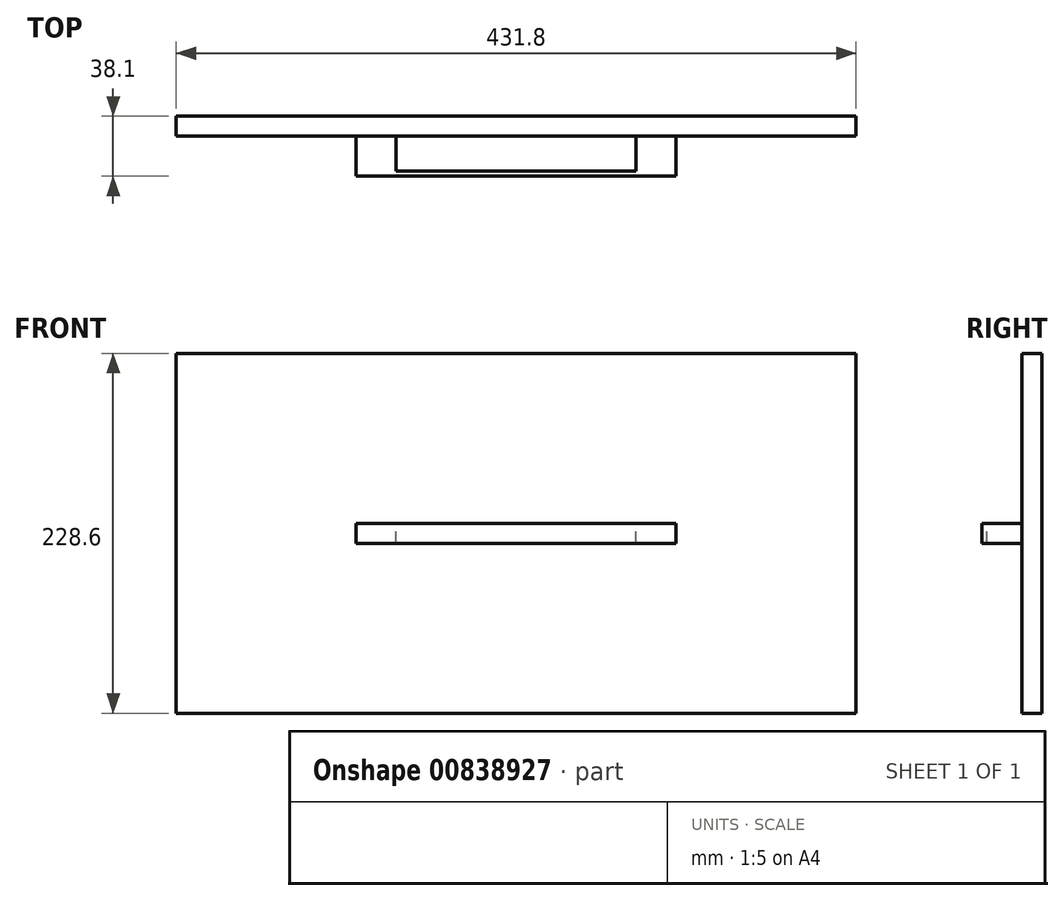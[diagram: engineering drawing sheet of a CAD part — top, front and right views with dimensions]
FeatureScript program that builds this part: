
annotation { "Feature Type Name" : "Feature", "Feature Type Description" : "" }
export const myFeature = defineFeature(function(context is Context, id is Id, definition is map)
    precondition{}
    {
        {
            var Q0;
            Q0=qCreatedBy(makeId("Front.planeOp"),FACE);
            var sketch = newSketch(context, id + "F0", { "sketchPlane" : qUnion([Q0])});
            skLineSegment(sketch, "E0", {"start": v(0, 0) * mm, "end": v(0, 228.6) * mm});
            skLineSegment(sketch, "E1", {"start": v(0, 228.6) * mm, "end": v(431.8, 228.6) * mm});
            skLineSegment(sketch, "E2", {"start": v(431.8, 228.6) * mm, "end": v(431.8, 0) * mm});
            skLineSegment(sketch, "E3", {"start": v(431.8, 0) * mm, "end": v(0, 0) * mm});
            skSolve(sketch);
        }
        {
            var Q0;
            Q0 = qSketchRegion(id + "F0", true);
            extrude(context, id + "F1", {"entities" : qUnion([Q0]), "depth" : 12.7 * mm, "offsetDistance" : 25.4 * mm});
        }
        {
            var Q0;
            Q0=makeQuery(id+"F1.opExtrude","CAP_FACE",FACE,{"disambiguationData":[OSD([sQuery(id+"F0.wireOp",EDGE,"E0"),sQuery(id+"F0.wireOp",EDGE,"E1"),sQuery(id+"F0.wireOp",EDGE,"E2"),sQuery(id+"F0.wireOp",EDGE,"E3")])],"isStart":false});
            var sketch = newSketch(context, id + "F2", { "sketchPlane" : qUnion([Q0])});
            skLineSegment(sketch, "E4", {"start": v(431.8, 228.6) * mm, "end": v(0, 0) * mm});
            skLineSegment(sketch, "E5", {"start": v(0, 228.6) * mm, "end": v(431.8, 0) * mm});
            skLineSegment(sketch, "E6", {"start": v(139.7, 114.3) * mm, "end": v(139.7, 120.65) * mm});
            skLineSegment(sketch, "E7", {"start": v(139.7, 120.65) * mm, "end": v(114.3, 120.65) * mm});
            skLineSegment(sketch, "E8", {"start": v(114.3, 120.65) * mm, "end": v(114.3, 114.3) * mm});
            skLineSegment(sketch, "E9", {"start": v(114.3, 114.3) * mm, "end": v(114.3, 107.95) * mm});
            skLineSegment(sketch, "E10", {"start": v(114.3, 107.95) * mm, "end": v(139.7, 107.95) * mm});
            skLineSegment(sketch, "E11", {"start": v(139.7, 107.95) * mm, "end": v(139.7, 114.3) * mm});
            skLineSegment(sketch, "E12.MirrorCS", {"start": v(292.1, 120.65) * mm, "end": v(317.5, 120.65) * mm});
            skLineSegment(sketch, "E13.MirrorCS", {"start": v(317.5, 107.95) * mm, "end": v(292.1, 107.95) * mm});
            skLineSegment(sketch, "E14.MirrorCS", {"start": v(317.5, 120.65) * mm, "end": v(317.5, 114.3) * mm});
            skLineSegment(sketch, "E15.MirrorCS", {"start": v(317.5, 114.3) * mm, "end": v(317.5, 107.95) * mm});
            skLineSegment(sketch, "E16.MirrorCS", {"start": v(292.1, 114.3) * mm, "end": v(292.1, 120.65) * mm});
            skLineSegment(sketch, "E17.MirrorCS", {"start": v(292.1, 107.95) * mm, "end": v(292.1, 114.3) * mm});
            skSolve(sketch);
        }
        {
            var Q0;
            Q0 = qSketchRegion(id + "F2", true);
            extrude(context, id + "F3", {"entities" : qUnion([Q0]), "operationType" : NewBodyOperationType.ADD, "depth" : 22.22 * mm, "offsetDistance" : 25.4 * mm});
        }
        {
            var Q0;
            Q0=makeQuery(id+"F3.opExtrude","SWEPT_FACE",FACE,{"disambiguationData":[OSD([sQuery(id+"F2.wireOp",EDGE,"E14.MirrorCS"),sQuery(id+"F2.wireOp",EDGE,"E15.MirrorCS")])]});
            var sketch = newSketch(context, id + "F4", { "sketchPlane" : qUnion([Q0])});
            skLineSegment(sketch, "E18", {"start": v(-34.93, 120.65) * mm, "end": v(-38.1, 120.65) * mm});
            skLineSegment(sketch, "E19", {"start": v(-38.1, 120.65) * mm, "end": v(-38.1, 107.95) * mm});
            skLineSegment(sketch, "E20", {"start": v(-38.1, 107.95) * mm, "end": v(-34.93, 107.95) * mm});
            skLineSegment(sketch, "E21", {"start": v(-34.93, 107.95) * mm, "end": v(-34.93, 120.65) * mm});
            skSolve(sketch);
        }
        {
            var Q0;
            Q0 = qSketchRegion(id + "F4", true);
            var Q1;
            Q1=makeQuery(id+"F3.opExtrude","SWEPT_FACE",FACE,{"disambiguationData":[OSD([sQuery(id+"F2.wireOp",EDGE,"E8"),sQuery(id+"F2.wireOp",EDGE,"E9")])]});
            extrude(context, id + "F5", {"entities" : qUnion([Q0]), "operationType" : NewBodyOperationType.ADD, "endBound" : BoundingType.UP_TO_SURFACE, "oppositeDirection" : true, "depth" : 25.4 * mm, "endBoundEntityFace" : qUnion([Q1]), "offsetDistance" : 25.4 * mm});
        }
    });
